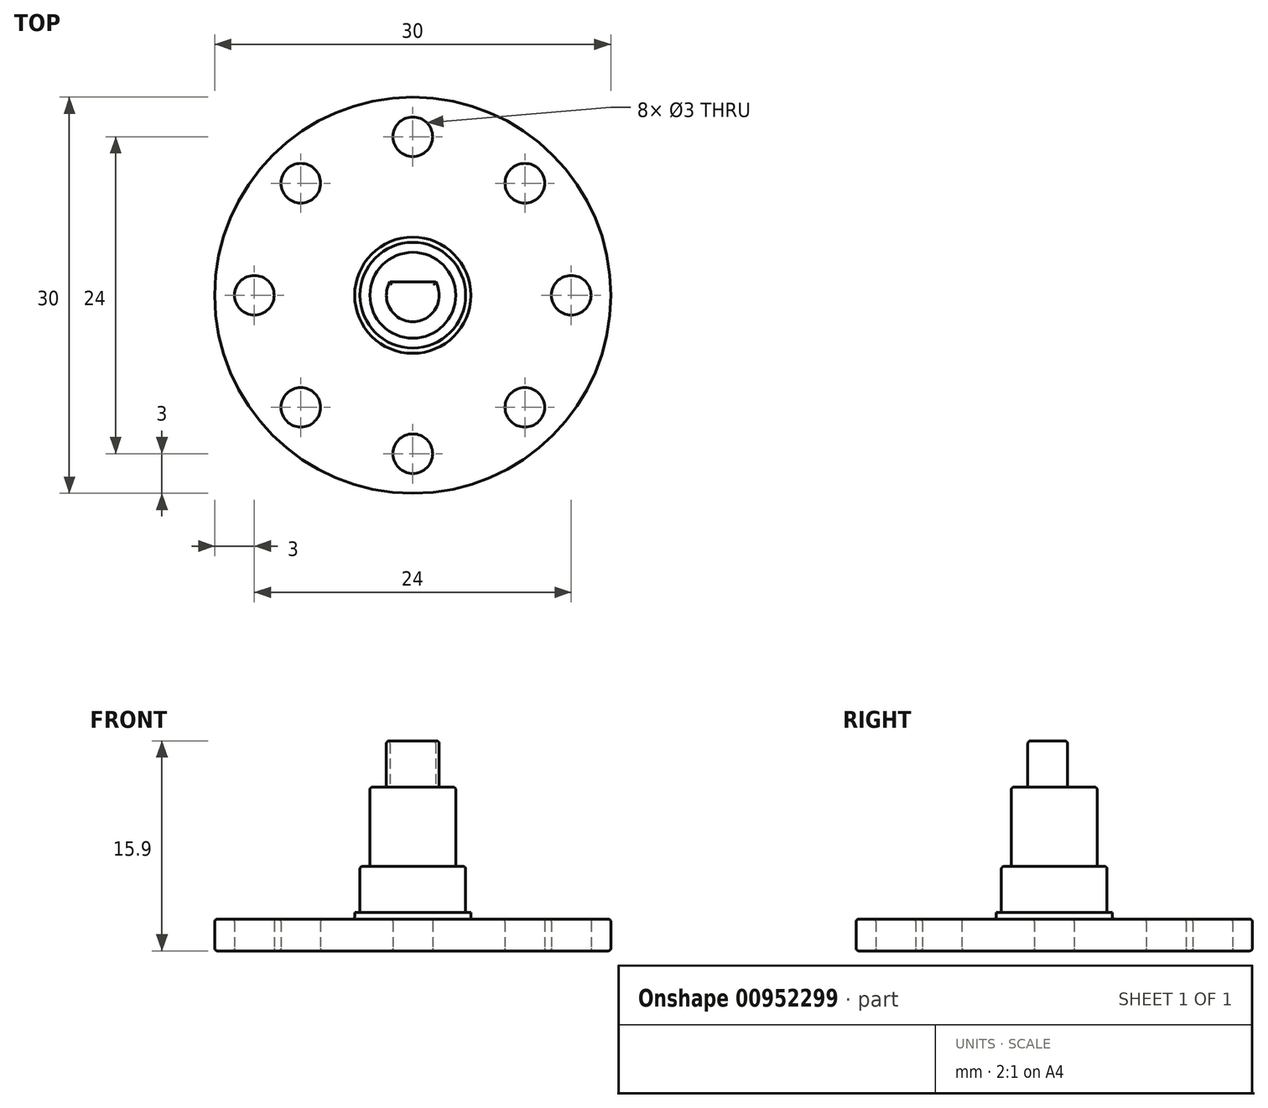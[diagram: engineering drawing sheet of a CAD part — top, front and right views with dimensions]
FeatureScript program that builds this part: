
annotation { "Feature Type Name" : "Feature", "Feature Type Description" : "" }
export const myFeature = defineFeature(function(context is Context, id is Id, definition is map)
    precondition{}
    {
        {
            var Q0;
            Q0=qCreatedBy(makeId("Top.planeOp"),FACE);
            var sketch = newSketch(context, id + "F0", { "sketchPlane" : qUnion([Q0])});
            skCircle(sketch, "E0", {"center": v(0, 0) * mm, "radius": 15 * mm});
            skCircle(sketch, "E1", {"center": v(0, 12) * mm, "radius": 1.5 * mm});
            skCircle(sketch, "E2.1.0", {"center": v(-8.49, 8.49) * mm, "radius": 1.5 * mm});
            skCircle(sketch, "E2.2.0", {"center": v(-12, 0) * mm, "radius": 1.5 * mm});
            skCircle(sketch, "E2.3.0", {"center": v(-8.49, -8.49) * mm, "radius": 1.5 * mm});
            skCircle(sketch, "E2.4.0", {"center": v(0, -12) * mm, "radius": 1.5 * mm});
            skCircle(sketch, "E2.5.0", {"center": v(8.49, -8.49) * mm, "radius": 1.5 * mm});
            skCircle(sketch, "E2.6.0", {"center": v(12, 0) * mm, "radius": 1.5 * mm});
            skCircle(sketch, "E2.7.0", {"center": v(8.49, 8.49) * mm, "radius": 1.5 * mm});
            skSolve(sketch);
        }
        {
            var Q0;
            Q0=makeQuery(id+"F0.imprint","IMPRINT",FACE,{"disambiguationData":[TD([[makeQuery(id+"F0.imprint","IMPRINT",EDGE,{"derivedFrom":sQuery(id+"F0.wireOp",EDGE,"E0")}),1.0]])]});
            extrude(context, id + "F1", {"entities" : qUnion([Q0]), "depth" : 2.4 * mm, "offsetDistance" : 25 * mm});
        }
        {
            var Q0;
            Q0=makeQuery(id+"F1.opExtrude","CAP_FACE",FACE,{"disambiguationData":[OSD([sQuery(id+"F0.wireOp",EDGE,"E0"),sQuery(id+"F0.wireOp",EDGE,"E1"),sQuery(id+"F0.wireOp",EDGE,"101f4eba-e25a-47fb-bb04-38ce5adc325e.1.0"),sQuery(id+"F0.wireOp",EDGE,"101f4eba-e25a-47fb-bb04-38ce5adc325e.2.0"),sQuery(id+"F0.wireOp",EDGE,"101f4eba-e25a-47fb-bb04-38ce5adc325e.3.0")])],"isStart":false});
            var sketch = newSketch(context, id + "F2", { "sketchPlane" : qUnion([Q0])});
            skCircle(sketch, "E3", {"center": v(0, 0) * mm, "radius": 4 * mm});
            skSolve(sketch);
        }
        {
            var Q0;
            Q0 = qSketchRegion(id + "F2", true);
            extrude(context, id + "F3", {"entities" : qUnion([Q0]), "operationType" : NewBodyOperationType.ADD, "depth" : 4 * mm, "offsetDistance" : 25 * mm});
        }
        {
            var Q0;
            Q0=makeQuery(id+"F1.opExtrude","CAP_FACE",FACE,{"disambiguationData":[OSD([sQuery(id+"F0.wireOp",EDGE,"E0"),sQuery(id+"F0.wireOp",EDGE,"E1"),sQuery(id+"F0.wireOp",EDGE,"E2.1.0"),sQuery(id+"F0.wireOp",EDGE,"E2.2.0"),sQuery(id+"F0.wireOp",EDGE,"E2.3.0"),sQuery(id+"F0.wireOp",EDGE,"E2.4.0"),sQuery(id+"F0.wireOp",EDGE,"E2.5.0"),sQuery(id+"F0.wireOp",EDGE,"E2.6.0"),sQuery(id+"F0.wireOp",EDGE,"E2.7.0")])],"isStart":false});
            var sketch = newSketch(context, id + "F4", { "sketchPlane" : qUnion([Q0])});
            skCircle(sketch, "E4", {"center": v(0, 0) * mm, "radius": 4.4 * mm});
            skSolve(sketch);
        }
        {
            var Q0;
            Q0 = qSketchRegion(id + "F4", true);
            extrude(context, id + "F5", {"entities" : qUnion([Q0]), "operationType" : NewBodyOperationType.ADD, "depth" : 0.5 * mm, "offsetDistance" : 25 * mm});
        }
        {
            var Q0;
            Q0=makeQuery(id+"F3.opExtrude","CAP_FACE",FACE,{"disambiguationData":[OSD([sQuery(id+"F2.wireOp",EDGE,"E3")])],"isStart":false});
            var sketch = newSketch(context, id + "F6", { "sketchPlane" : qUnion([Q0])});
            skLineSegment(sketch, "E5", {"start": v(-3.87, 1) * mm, "end": v(3.87, 1) * mm});
            skCircle(sketch, "E6", {"center": v(0, 0) * mm, "radius": 2 * mm});
            skSolve(sketch);
        }
        {
            var Q0;
            {var subQ0=sQuery(id+"F6.wireOp",EDGE,"E6");var subQ1=sQuery(id+"F6.wireOp",EDGE,"E5");var subQ2=makeQuery(id+"F6.imprint","INTERSECT",VERTEX,{"disambiguationData":[OD(0.0)],"derivedFrom":[subQ1,subQ0]});Q0=makeQuery(id+"F6.imprint","IMPRINT",FACE,{"disambiguationData":[TD([[makeQuery(id+"F6.imprint","IMPRINT",EDGE,{"disambiguationData":[TD([[subQ2,-1.0]])],"derivedFrom":subQ1}),-1.0]])]});}
            extrude(context, id + "F7", {"entities" : qUnion([Q0]), "operationType" : NewBodyOperationType.ADD, "depth" : 9.5 * mm, "offsetDistance" : 25 * mm});
        }
        {
            var Q0;
            {var subQ0=sQuery(id+"F6.wireOp",EDGE,"E5");var subQ1=makeQuery(id+"F3.opExtrude","CAP_EDGE",EDGE,{"disambiguationData":[OSD([sQuery(id+"F2.wireOp",EDGE,"E3")])],"isStart":false});var subQ2=makeQuery(id+"F6.imprint","INTERSECT",VERTEX,{"disambiguationData":[OD(0.0)],"derivedFrom":[subQ1,subQ0]});Q0=makeQuery(id+"F6.imprint","IMPRINT",FACE,{"disambiguationData":[TD([[makeQuery(id+"F6.imprint","IMPRINT",EDGE,{"disambiguationData":[TD([[subQ2,-1.0]])],"derivedFrom":subQ0}),-1.0]])]});}
            var sketch = newSketch(context, id + "F8", { "sketchPlane" : qUnion([Q0])});
            skCircle(sketch, "E7", {"center": v(0, 0) * mm, "radius": 3.25 * mm});
            skSolve(sketch);
        }
        {
            var Q0;
            Q0 = qSketchRegion(id + "F8", true);
            extrude(context, id + "F9", {"entities" : qUnion([Q0]), "operationType" : NewBodyOperationType.ADD, "depth" : 6 * mm, "offsetDistance" : 25 * mm});
        }
        {
            var Q0;
            Q0=makeQuery(id+"F7.opExtrude","CAP_FACE",FACE,{"disambiguationData":[OSD([sQuery(id+"F6.wireOp",EDGE,"E5"),sQuery(id+"F6.wireOp",EDGE,"E6")])],"isStart":false});
            var Q1;
            Q1=makeQuery(id+"F9.opExtrude","CAP_EDGE",EDGE,{"disambiguationData":[OSD([sQuery(id+"F8.wireOp",EDGE,"E7")])],"isStart":false});
            var Q2;
            Q2=makeQuery(id+"F3.opExtrude","CAP_EDGE",EDGE,{"disambiguationData":[OSD([sQuery(id+"F2.wireOp",EDGE,"E3")])],"isStart":false});
            var Q3;
            Q3=makeQuery(id+"F1.opExtrude","CAP_FACE",FACE,{"disambiguationData":[OSD([sQuery(id+"F0.wireOp",EDGE,"E0"),sQuery(id+"F0.wireOp",EDGE,"E1"),sQuery(id+"F0.wireOp",EDGE,"E2.1.0"),sQuery(id+"F0.wireOp",EDGE,"E2.2.0"),sQuery(id+"F0.wireOp",EDGE,"E2.3.0"),sQuery(id+"F0.wireOp",EDGE,"E2.4.0"),sQuery(id+"F0.wireOp",EDGE,"E2.5.0"),sQuery(id+"F0.wireOp",EDGE,"E2.6.0"),sQuery(id+"F0.wireOp",EDGE,"E2.7.0")])],"isStart":true});
            var Q4;
            Q4=makeQuery(id+"F1.opExtrude","CAP_FACE",FACE,{"disambiguationData":[OSD([sQuery(id+"F0.wireOp",EDGE,"E0"),sQuery(id+"F0.wireOp",EDGE,"E1"),sQuery(id+"F0.wireOp",EDGE,"E2.1.0"),sQuery(id+"F0.wireOp",EDGE,"E2.2.0"),sQuery(id+"F0.wireOp",EDGE,"E2.3.0"),sQuery(id+"F0.wireOp",EDGE,"E2.4.0"),sQuery(id+"F0.wireOp",EDGE,"E2.5.0"),sQuery(id+"F0.wireOp",EDGE,"E2.6.0"),sQuery(id+"F0.wireOp",EDGE,"E2.7.0")])],"isStart":false});
            fillet(context, id + "F10", {"entities" : qUnion([Q0, Q1, Q2, Q3, Q4]), "tangentPropagation" : true, "radius" : 0.2 * mm, "defaultsChanged" : false, "vertexSettings" : [], "allowEdgeOverflow" : false});
        }
    });
